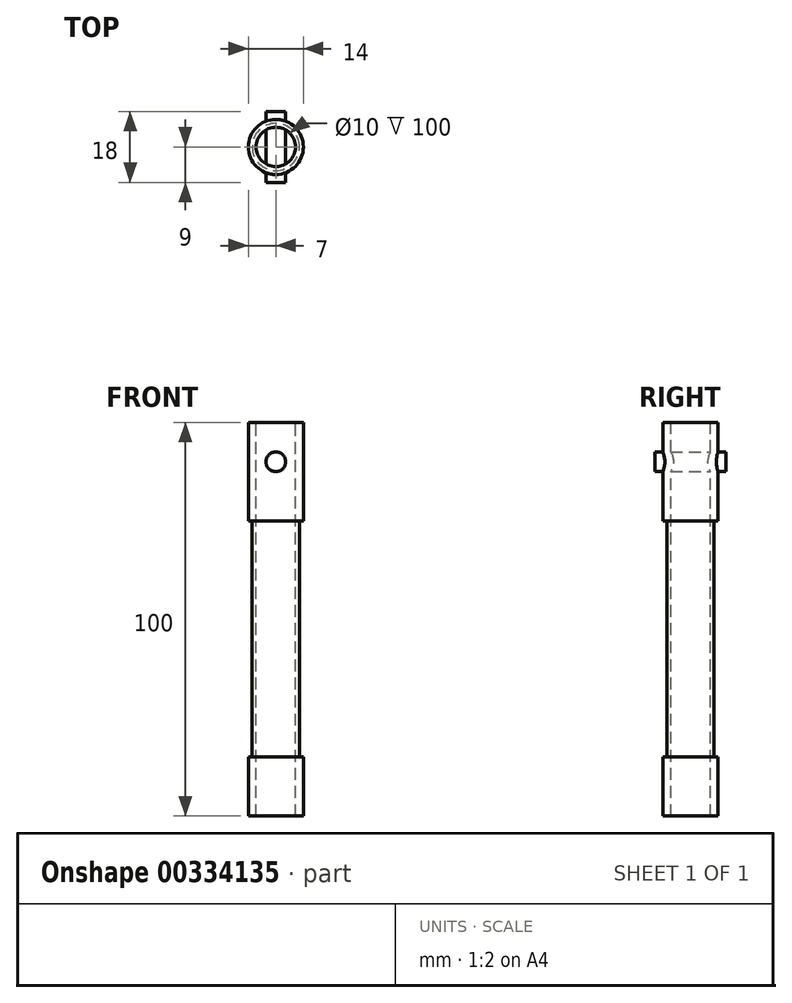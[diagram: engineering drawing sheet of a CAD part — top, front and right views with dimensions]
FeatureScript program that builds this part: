
annotation { "Feature Type Name" : "Feature", "Feature Type Description" : "" }
export const myFeature = defineFeature(function(context is Context, id is Id, definition is map)
    precondition{}
    {
        {
            var Q0;
            Q0=qCreatedBy(makeId("Front.planeOp"),FACE);
            var sketch = newSketch(context, id + "F0", { "sketchPlane" : qUnion([Q0])});
            skLineSegment(sketch, "E0", {"start": v(5, 31) * mm, "end": v(7, 31) * mm});
            skLineSegment(sketch, "E1", {"start": v(7, 31) * mm, "end": v(7, 6) * mm});
            skLineSegment(sketch, "E2", {"start": v(7, 6) * mm, "end": v(6, 6) * mm});
            skLineSegment(sketch, "E3", {"start": v(6, 6) * mm, "end": v(6, -54) * mm});
            skLineSegment(sketch, "E4", {"start": v(6, -54) * mm, "end": v(7, -54) * mm});
            skLineSegment(sketch, "E5", {"start": v(7, -54) * mm, "end": v(7, -69) * mm});
            skLineSegment(sketch, "E6", {"start": v(7, -69) * mm, "end": v(5, -69) * mm});
            skLineSegment(sketch, "E7", {"start": v(5, -69) * mm, "end": v(5, 31) * mm});
            skLineSegment(sketch, "E8", {"start": v(0, 36.07) * mm, "end": v(0, -81.1) * mm, "construction": true});
            skSolve(sketch);
        }
        {
            var Q0;
            Q0=qSketchRegion(id+"F0",true);
            var Q1;
            Q1=sQuery(id+"F0.wireOp",EDGE,"E8");
            revolve(context, id + "F1", {"entities" : qUnion([Q0]), "axis" : qUnion([Q1]), "revolveType" : RevolveType.FULL});
        }
        {
            var Q0;
            Q0=qCreatedBy(makeId("Front.planeOp"),FACE);
            var sketch = newSketch(context, id + "F2", { "sketchPlane" : qUnion([Q0])});
            skCircle(sketch, "E9", {"center": v(0, 21) * mm, "radius": 2.5 * mm});
            skSolve(sketch);
        }
        {
            var Q0;
            Q0=qSketchRegion(id+"F2",true);
            extrude(context, id + "F3", {"entities" : qUnion([Q0]), "operationType" : NewBodyOperationType.ADD, "depth" : 18 * mm, "symmetric" : true});
        }
    });
